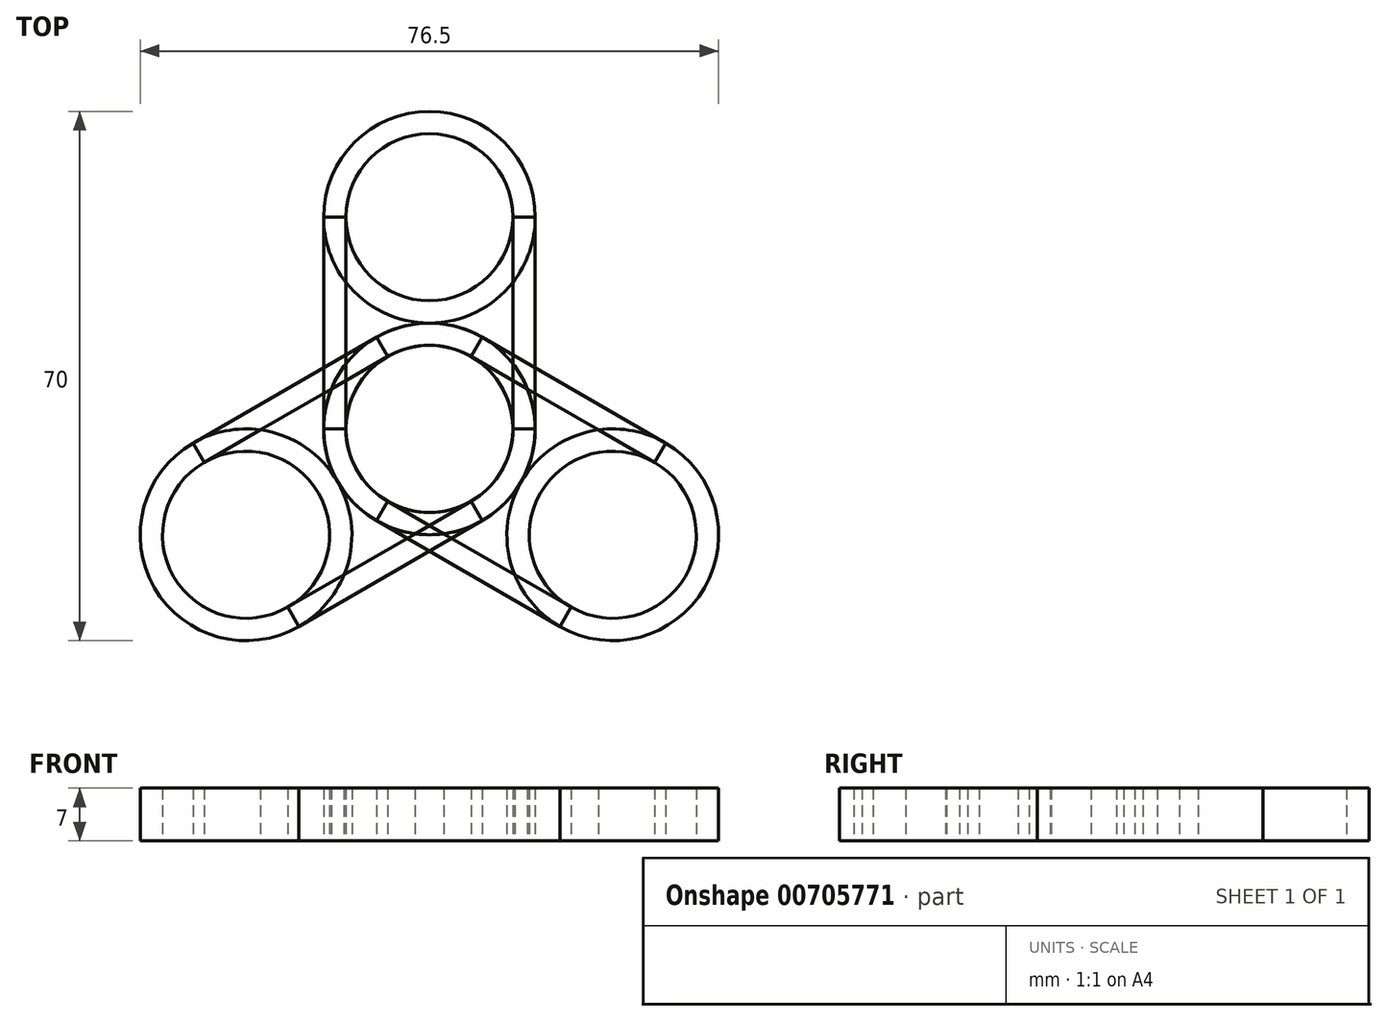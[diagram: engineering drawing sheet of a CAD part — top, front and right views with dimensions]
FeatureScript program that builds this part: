
annotation { "Feature Type Name" : "Feature", "Feature Type Description" : "" }
export const myFeature = defineFeature(function(context is Context, id is Id, definition is map)
    precondition{}
    {
        {
            var Q0;
            Q0=qCreatedBy(makeId("Top.planeOp"),FACE);
            var sketch = newSketch(context, id + "F0", { "sketchPlane" : qUnion([Q0])});
            skLineSegment(sketch, "E0.bottom", {"start": v(14, -14) * mm, "end": v(-14, -14) * mm});
            skLineSegment(sketch, "E0.top", {"start": v(14, 14) * mm, "end": v(-14, 14) * mm});
            skLineSegment(sketch, "E0.left", {"start": v(14, -14) * mm, "end": v(14, 14) * mm});
            skLineSegment(sketch, "E0.right", {"start": v(-14, -14) * mm, "end": v(-14, 14) * mm});
            skPoint(sketch, "E0.middle", {"position": v(0, 0) * mm});
            skCircle(sketch, "E1", {"center": v(0, 14) * mm, "radius": 14 * mm});
            skCircle(sketch, "E2", {"center": v(0, 14) * mm, "radius": 11.05 * mm});
            skCircle(sketch, "E3", {"center": v(0, -14) * mm, "radius": 14 * mm});
            skCircle(sketch, "E4", {"center": v(0, -14) * mm, "radius": 11.05 * mm});
            skLineSegment(sketch, "E5", {"start": v(11.05, 14) * mm, "end": v(11.05, -14) * mm});
            skLineSegment(sketch, "E6", {"start": v(-11.05, 14) * mm, "end": v(-11.05, -14) * mm});
            skSolve(sketch);
        }
        {
            var Q0;
            {var subQ4=sQuery(id+"F0.wireOp",EDGE,"E1");var subQ7=sQuery(id+"F0.wireOp",EDGE,"E6");var subQ9=makeQuery(id+"F0.imprint","INTERSECT",VERTEX,{"derivedFrom":[subQ4,subQ7]});Q0=makeQuery(id+"F0.imprint","IMPRINT",FACE,{"disambiguationData":[TD([[makeQuery(id+"F0.imprint","IMPRINT",EDGE,{"disambiguationData":[TD([[subQ9,-1.0]])],"derivedFrom":subQ4}),1.0]])]});}
            var Q1;
            {var subQ4=sQuery(id+"F0.wireOp",EDGE,"E3");var subQ8=makeQuery(id+"F0.imprint","INTERSECT",VERTEX,{"derivedFrom":[sQuery(id+"F0.wireOp",EDGE,"E1"),subQ4]});Q1=makeQuery(id+"F0.imprint","IMPRINT",FACE,{"disambiguationData":[TD([[makeQuery(id+"F0.imprint","IMPRINT",EDGE,{"disambiguationData":[TD([[subQ8,1.0]])],"derivedFrom":subQ4}),1.0]])]});}
            var Q2;
            {var subQ0=sQuery(id+"F0.wireOp",EDGE,"E3");var subQ1=sQuery(id+"F0.wireOp",EDGE,"E0.bottom");var subQ2=makeQuery(id+"F0.imprint","INTERSECT",VERTEX,{"derivedFrom":[subQ1,sQuery(id+"F0.wireOp",EDGE,"E0.left"),subQ0]});Q2=makeQuery(id+"F0.imprint","IMPRINT",FACE,{"disambiguationData":[TD([[makeQuery(id+"F0.imprint","IMPRINT",EDGE,{"disambiguationData":[TD([[subQ2,-1.0]])],"derivedFrom":subQ1}),1.0]])]});}
            var Q3;
            {var subQ0=sQuery(id+"F0.wireOp",EDGE,"E1");var subQ1=sQuery(id+"F0.wireOp",EDGE,"E0.top");var subQ2=makeQuery(id+"F0.imprint","INTERSECT",VERTEX,{"derivedFrom":[subQ1,sQuery(id+"F0.wireOp",EDGE,"E0.left"),subQ0]});Q3=makeQuery(id+"F0.imprint","IMPRINT",FACE,{"disambiguationData":[TD([[makeQuery(id+"F0.imprint","IMPRINT",EDGE,{"disambiguationData":[TD([[subQ2,-1.0]])],"derivedFrom":subQ1}),-1.0]])]});}
            var Q4;
            {var subQ0=sQuery(id+"F0.wireOp",EDGE,"E0.left");Q4=makeQuery(id+"F0.imprint","IMPRINT",FACE,{"disambiguationData":[TD([[makeQuery(id+"F0.imprint","IMPRINT",EDGE,{"derivedFrom":subQ0}),1.0]])]});}
            var Q5;
            {var subQ0=sQuery(id+"F0.wireOp",EDGE,"E0.right");Q5=makeQuery(id+"F0.imprint","IMPRINT",FACE,{"disambiguationData":[TD([[makeQuery(id+"F0.imprint","IMPRINT",EDGE,{"derivedFrom":subQ0}),-1.0]])]});}
            extrude(context, id + "F1", {"entities" : qUnion([Q0, Q1, Q2, Q3, Q4, Q5]), "depth" : 7 * mm, "offsetDistance" : 25 * mm});
        }
        {
            var Q0;
            {var subQ0=sQuery(id+"F0.wireOp",EDGE,"E1");var subQ3=sQuery(id+"F0.wireOp",EDGE,"E5");var subQ5=makeQuery(id+"F0.imprint","INTERSECT",VERTEX,{"derivedFrom":[subQ0,subQ3]});Q0=makeQuery(id+"F0.imprint","IMPRINT",FACE,{"disambiguationData":[TD([[makeQuery(id+"F0.imprint","IMPRINT",EDGE,{"disambiguationData":[TD([[subQ5,-1.0]])],"derivedFrom":subQ0}),1.0]])]});}
            var Q1;
            {var subQ0=sQuery(id+"F0.wireOp",EDGE,"E3");var subQ3=sQuery(id+"F0.wireOp",EDGE,"E5");var subQ5=makeQuery(id+"F0.imprint","INTERSECT",VERTEX,{"derivedFrom":[subQ0,subQ3]});Q1=makeQuery(id+"F0.imprint","IMPRINT",FACE,{"disambiguationData":[TD([[makeQuery(id+"F0.imprint","IMPRINT",EDGE,{"disambiguationData":[TD([[subQ5,1.0]])],"derivedFrom":subQ0}),1.0]])]});}
            var Q2;
            {var subQ0=sQuery(id+"F0.wireOp",EDGE,"E3");var subQ3=sQuery(id+"F0.wireOp",EDGE,"E6");var subQ5=makeQuery(id+"F0.imprint","INTERSECT",VERTEX,{"derivedFrom":[subQ0,subQ3]});Q2=makeQuery(id+"F0.imprint","IMPRINT",FACE,{"disambiguationData":[TD([[makeQuery(id+"F0.imprint","IMPRINT",EDGE,{"disambiguationData":[TD([[subQ5,-1.0]])],"derivedFrom":subQ0}),1.0]])]});}
            var Q3;
            {var subQ0=sQuery(id+"F0.wireOp",EDGE,"E1");var subQ3=sQuery(id+"F0.wireOp",EDGE,"E6");var subQ5=makeQuery(id+"F0.imprint","INTERSECT",VERTEX,{"derivedFrom":[subQ0,subQ3]});Q3=makeQuery(id+"F0.imprint","IMPRINT",FACE,{"disambiguationData":[TD([[makeQuery(id+"F0.imprint","IMPRINT",EDGE,{"disambiguationData":[TD([[subQ5,1.0]])],"derivedFrom":subQ0}),1.0]])]});}
            extrude(context, id + "F2", {"entities" : qUnion([Q0, Q1, Q2, Q3]), "depth" : 7 * mm, "offsetDistance" : 25 * mm});
        }
        {
            var Q0;
            Q0=makeQuery(id+"F1.opExtrude","SWEPT_BODY",BODY,{"disambiguationData":[OSD([sQuery(id+"F0.wireOp",EDGE,"E1"),sQuery(id+"F0.wireOp",EDGE,"E2"),sQuery(id+"F0.wireOp",EDGE,"E5"),sQuery(id+"F0.wireOp",EDGE,"E6")])]});
            var Q1;
            Q1=makeQuery(id+"F1.opExtrude","SWEPT_BODY",BODY,{"disambiguationData":[OSD([sQuery(id+"F0.wireOp",EDGE,"E0.right"),sQuery(id+"F0.wireOp",EDGE,"E1"),sQuery(id+"F0.wireOp",EDGE,"E3"),sQuery(id+"F0.wireOp",EDGE,"E6")])]});
            var Q2;
            Q2=makeQuery(id+"F1.opExtrude","SWEPT_BODY",BODY,{"disambiguationData":[OSD([sQuery(id+"F0.wireOp",EDGE,"E0.top"),sQuery(id+"F0.wireOp",EDGE,"E1"),sQuery(id+"F0.wireOp",EDGE,"E2")])]});
            var Q3;
            Q3=makeQuery(id+"F1.opExtrude","SWEPT_BODY",BODY,{"disambiguationData":[OSD([sQuery(id+"F0.wireOp",EDGE,"E0.left"),sQuery(id+"F0.wireOp",EDGE,"E1"),sQuery(id+"F0.wireOp",EDGE,"E3"),sQuery(id+"F0.wireOp",EDGE,"E5")])]});
            var Q4;
            Q4=makeQuery(id+"F1.opExtrude","SWEPT_BODY",BODY,{"disambiguationData":[OSD([sQuery(id+"F0.wireOp",EDGE,"E0.bottom"),sQuery(id+"F0.wireOp",EDGE,"E3"),sQuery(id+"F0.wireOp",EDGE,"E4")])]});
            var Q5;
            Q5=makeQuery(id+"F1.opExtrude","SWEPT_BODY",BODY,{"disambiguationData":[OSD([sQuery(id+"F0.wireOp",EDGE,"E3"),sQuery(id+"F0.wireOp",EDGE,"E4"),sQuery(id+"F0.wireOp",EDGE,"E5"),sQuery(id+"F0.wireOp",EDGE,"E6")])]});
            var Q6;
            Q6=makeQuery(id+"F2.opExtrude","SWEPT_BODY",BODY,{"disambiguationData":[OSD([sQuery(id+"F0.wireOp",EDGE,"E0.bottom"),sQuery(id+"F0.wireOp",EDGE,"E3"),sQuery(id+"F0.wireOp",EDGE,"E5")])]});
            var Q7;
            Q7=makeQuery(id+"F2.opExtrude","SWEPT_BODY",BODY,{"disambiguationData":[OSD([sQuery(id+"F0.wireOp",EDGE,"E0.bottom"),sQuery(id+"F0.wireOp",EDGE,"E3"),sQuery(id+"F0.wireOp",EDGE,"E6")])]});
            var Q8;
            Q8=makeQuery(id+"F2.opExtrude","SWEPT_BODY",BODY,{"disambiguationData":[OSD([sQuery(id+"F0.wireOp",EDGE,"E0.top"),sQuery(id+"F0.wireOp",EDGE,"E1"),sQuery(id+"F0.wireOp",EDGE,"E5")])]});
            var Q9;
            Q9=makeQuery(id+"F2.opExtrude","SWEPT_BODY",BODY,{"disambiguationData":[OSD([sQuery(id+"F0.wireOp",EDGE,"E0.top"),sQuery(id+"F0.wireOp",EDGE,"E1"),sQuery(id+"F0.wireOp",EDGE,"E6")])]});
            var Q10;
            Q10=sQuery(id+"F0.wireOp",EDGE,"E3");
            circularPattern(context, id + "F3", {"entities" : qUnion([Q0, Q1, Q2, Q3, Q4, Q5, Q6, Q7, Q8, Q9]), "axis" : qUnion([Q10]), "angle" : 360 * degree, "instanceCount" : 3, "equalSpace" : true});
        }
    });
